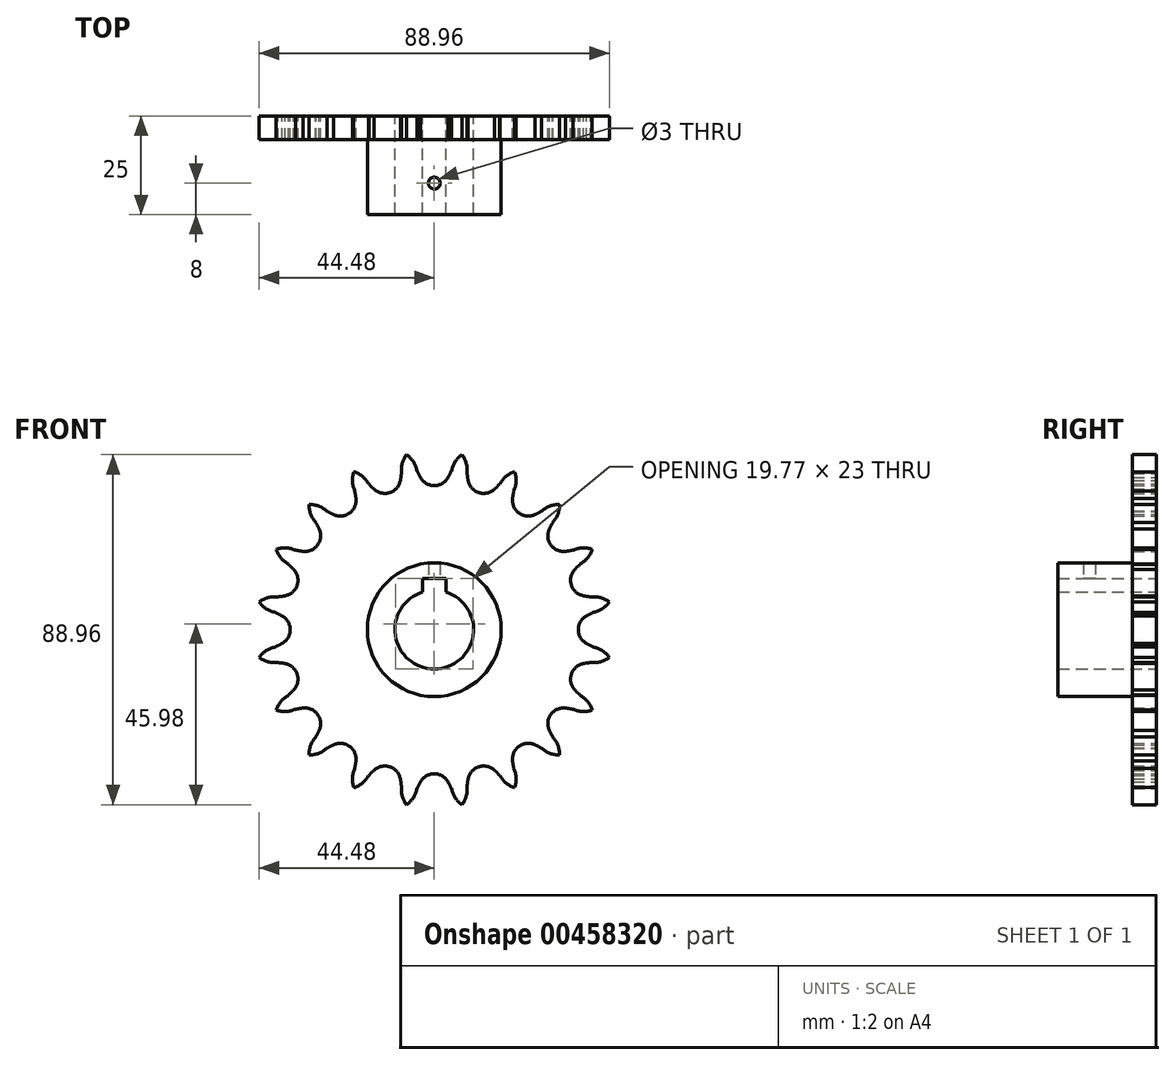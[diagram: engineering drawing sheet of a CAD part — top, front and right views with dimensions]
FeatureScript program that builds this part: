
annotation { "Feature Type Name" : "Feature", "Feature Type Description" : "" }
export const myFeature = defineFeature(function(context is Context, id is Id, definition is map)
    precondition{}
    {
        {
            var Q0;
            Q0=qCreatedBy(makeId("Front.planeOp"),FACE);
            var sketch = newSketch(context, id + "F0", { "sketchPlane" : qUnion([Q0])});
            skCircle(sketch, "E0", {"center": v(0, 0) * mm, "radius": 17 * mm});
            skCircle(sketch, "E1", {"center": v(0, 0) * mm, "radius": 40.6 * mm});
            skLineSegment(sketch, "E2", {"start": v(0, 0) * mm, "end": v(0, 40.6) * mm, "construction": true});
            skArc(sketch, "E3", {"start": v(3.98, 40.4) * mm, "mid": v(3.98, 40.5) * mm, "end": v(3.98, 40.6) * mm});
            skLineSegment(sketch, "E4", {"start": v(0, 40.6) * mm, "end": v(42.62, 40.6) * mm, "construction": true});
            skLineSegment(sketch, "E5", {"start": v(0, 40.6) * mm, "end": v(4.45, 44.07) * mm, "construction": true});
            skArc(sketch, "E6", {"start": v(-4.39, 40.35) * mm, "mid": v(-5.32, 42.68) * mm, "end": v(-7.05, 44.48) * mm});
            skLineSegment(sketch, "E7", {"start": v(4.45, 44.07) * mm, "end": v(-4.39, 40.35) * mm, "construction": true});
            skLineSegment(sketch, "E8", {"start": v(0, 0) * mm, "end": v(-7.48, 47.24) * mm, "construction": true});
            skLineSegment(sketch, "E9", {"start": v(4.45, 44.07) * mm, "end": v(-3.14, 38.14) * mm, "construction": true});
            skArc(sketch, "E10.trimOffspring", {"start": v(3.14, 43.04) * mm, "mid": v(3, 43.22) * mm, "end": v(2.83, 43.39) * mm});
            skArc(sketch, "E11.trimOffspring", {"start": v(-3.98, 40.52) * mm, "mid": v(-3.98, 40.46) * mm, "end": v(-3.98, 40.4) * mm});
            skArc(sketch, "E12.trimOffspring", {"start": v(-3.5, 38.7) * mm, "mid": v(-2.04, 37.17) * mm, "end": v(0, 36.61) * mm});
            skArc(sketch, "E13.trimOffspring", {"start": v(-4.56, 41.04) * mm, "mid": v(-3.96, 39.54) * mm, "end": v(-3.14, 38.14) * mm});
            skArc(sketch, "E14.MirrorCS", {"start": v(3.5, 38.7) * mm, "mid": v(2.04, 37.17) * mm, "end": v(0, 36.61) * mm});
            skArc(sketch, "E15.MirrorCS", {"start": v(4.56, 41.04) * mm, "mid": v(3.96, 39.54) * mm, "end": v(3.14, 38.14) * mm});
            skArc(sketch, "E16.MirrorCS", {"start": v(4.39, 40.35) * mm, "mid": v(5.32, 42.68) * mm, "end": v(7.05, 44.48) * mm});
            skArc(sketch, "E17.1.0", {"start": v(-8.3, 39.73) * mm, "mid": v(-8.13, 42.23) * mm, "end": v(-7.05, 44.48) * mm});
            skArc(sketch, "E17.1.1", {"start": v(-8.35, 40.44) * mm, "mid": v(-8.45, 38.83) * mm, "end": v(-8.8, 37.24) * mm});
            skArc(sketch, "E17.1.2", {"start": v(-8.63, 37.88) * mm, "mid": v(-9.55, 35.98) * mm, "end": v(-11.31, 34.82) * mm});
            skArc(sketch, "E17.1.3", {"start": v(-15.29, 35.72) * mm, "mid": v(-13.42, 34.72) * mm, "end": v(-11.31, 34.82) * mm});
            skArc(sketch, "E17.1.4", {"start": v(-17.02, 37.63) * mm, "mid": v(-15.99, 36.38) * mm, "end": v(-14.77, 35.3) * mm});
            skArc(sketch, "E17.1.5", {"start": v(-16.64, 37.02) * mm, "mid": v(-18.24, 38.94) * mm, "end": v(-20.45, 40.13) * mm});
            skArc(sketch, "E17.2.0", {"start": v(-20.17, 35.23) * mm, "mid": v(-20.78, 37.65) * mm, "end": v(-20.45, 40.13) * mm});
            skArc(sketch, "E17.2.1", {"start": v(-20.44, 35.88) * mm, "mid": v(-20.03, 34.31) * mm, "end": v(-19.88, 32.7) * mm});
            skArc(sketch, "E17.2.2", {"start": v(-19.91, 33.36) * mm, "mid": v(-20.2, 31.27) * mm, "end": v(-21.52, 29.62) * mm});
            skArc(sketch, "E17.2.3", {"start": v(-25.58, 29.25) * mm, "mid": v(-23.5, 28.87) * mm, "end": v(-21.52, 29.62) * mm});
            skArc(sketch, "E17.2.4", {"start": v(-27.81, 30.53) * mm, "mid": v(-26.44, 29.66) * mm, "end": v(-24.96, 29.01) * mm});
            skArc(sketch, "E17.2.5", {"start": v(-27.27, 30.07) * mm, "mid": v(-29.38, 31.4) * mm, "end": v(-31.85, 31.85) * mm});
            skArc(sketch, "E17.3.0", {"start": v(-30.07, 27.27) * mm, "mid": v(-31.4, 29.38) * mm, "end": v(-31.85, 31.85) * mm});
            skArc(sketch, "E17.3.1", {"start": v(-30.53, 27.81) * mm, "mid": v(-29.66, 26.44) * mm, "end": v(-29.01, 24.96) * mm});
            skArc(sketch, "E17.3.2", {"start": v(-29.25, 25.58) * mm, "mid": v(-28.87, 23.5) * mm, "end": v(-29.62, 21.52) * mm});
            skArc(sketch, "E17.3.3", {"start": v(-33.36, 19.91) * mm, "mid": v(-31.27, 20.2) * mm, "end": v(-29.62, 21.52) * mm});
            skArc(sketch, "E17.3.4", {"start": v(-35.88, 20.44) * mm, "mid": v(-34.31, 20.03) * mm, "end": v(-32.7, 19.88) * mm});
            skArc(sketch, "E17.3.5", {"start": v(-35.23, 20.17) * mm, "mid": v(-37.65, 20.78) * mm, "end": v(-40.13, 20.45) * mm});
            skArc(sketch, "E17.4.0", {"start": v(-37.02, 16.64) * mm, "mid": v(-38.94, 18.24) * mm, "end": v(-40.13, 20.45) * mm});
            skArc(sketch, "E17.4.1", {"start": v(-37.63, 17.02) * mm, "mid": v(-36.38, 15.99) * mm, "end": v(-35.3, 14.77) * mm});
            skArc(sketch, "E17.4.2", {"start": v(-35.72, 15.29) * mm, "mid": v(-34.72, 13.42) * mm, "end": v(-34.82, 11.31) * mm});
            skArc(sketch, "E17.4.3", {"start": v(-37.88, 8.63) * mm, "mid": v(-35.98, 9.55) * mm, "end": v(-34.82, 11.31) * mm});
            skArc(sketch, "E17.4.4", {"start": v(-40.44, 8.35) * mm, "mid": v(-38.83, 8.45) * mm, "end": v(-37.24, 8.8) * mm});
            skArc(sketch, "E17.4.5", {"start": v(-39.73, 8.3) * mm, "mid": v(-42.23, 8.13) * mm, "end": v(-44.48, 7.05) * mm});
            skArc(sketch, "E17.5.0", {"start": v(-40.35, 4.39) * mm, "mid": v(-42.68, 5.32) * mm, "end": v(-44.48, 7.05) * mm});
            skArc(sketch, "E17.5.1", {"start": v(-41.04, 4.56) * mm, "mid": v(-39.54, 3.96) * mm, "end": v(-38.14, 3.14) * mm});
            skArc(sketch, "E17.5.2", {"start": v(-38.7, 3.5) * mm, "mid": v(-37.17, 2.04) * mm, "end": v(-36.61, 0) * mm});
            skArc(sketch, "E17.5.3", {"start": v(-38.7, -3.5) * mm, "mid": v(-37.17, -2.04) * mm, "end": v(-36.61, 0) * mm});
            skArc(sketch, "E17.5.4", {"start": v(-41.04, -4.56) * mm, "mid": v(-39.54, -3.96) * mm, "end": v(-38.14, -3.14) * mm});
            skArc(sketch, "E17.5.5", {"start": v(-40.35, -4.39) * mm, "mid": v(-42.68, -5.32) * mm, "end": v(-44.48, -7.05) * mm});
            skArc(sketch, "E17.6.0", {"start": v(-39.73, -8.3) * mm, "mid": v(-42.23, -8.13) * mm, "end": v(-44.48, -7.05) * mm});
            skArc(sketch, "E17.6.1", {"start": v(-40.44, -8.35) * mm, "mid": v(-38.83, -8.45) * mm, "end": v(-37.24, -8.8) * mm});
            skArc(sketch, "E17.6.2", {"start": v(-37.88, -8.63) * mm, "mid": v(-35.98, -9.55) * mm, "end": v(-34.82, -11.31) * mm});
            skArc(sketch, "E17.6.3", {"start": v(-35.72, -15.29) * mm, "mid": v(-34.72, -13.42) * mm, "end": v(-34.82, -11.31) * mm});
            skArc(sketch, "E17.6.4", {"start": v(-37.63, -17.02) * mm, "mid": v(-36.38, -15.99) * mm, "end": v(-35.3, -14.77) * mm});
            skArc(sketch, "E17.6.5", {"start": v(-37.02, -16.64) * mm, "mid": v(-38.94, -18.24) * mm, "end": v(-40.13, -20.45) * mm});
            skArc(sketch, "E17.7.0", {"start": v(-35.23, -20.17) * mm, "mid": v(-37.65, -20.78) * mm, "end": v(-40.13, -20.45) * mm});
            skArc(sketch, "E17.7.1", {"start": v(-35.88, -20.44) * mm, "mid": v(-34.31, -20.03) * mm, "end": v(-32.7, -19.88) * mm});
            skArc(sketch, "E17.7.2", {"start": v(-33.36, -19.91) * mm, "mid": v(-31.27, -20.2) * mm, "end": v(-29.62, -21.52) * mm});
            skArc(sketch, "E17.7.3", {"start": v(-29.25, -25.58) * mm, "mid": v(-28.87, -23.5) * mm, "end": v(-29.62, -21.52) * mm});
            skArc(sketch, "E17.7.4", {"start": v(-30.53, -27.81) * mm, "mid": v(-29.66, -26.44) * mm, "end": v(-29.01, -24.96) * mm});
            skArc(sketch, "E17.7.5", {"start": v(-30.07, -27.27) * mm, "mid": v(-31.4, -29.38) * mm, "end": v(-31.85, -31.85) * mm});
            skArc(sketch, "E17.8.0", {"start": v(-27.27, -30.07) * mm, "mid": v(-29.38, -31.4) * mm, "end": v(-31.85, -31.85) * mm});
            skArc(sketch, "E17.8.1", {"start": v(-27.81, -30.53) * mm, "mid": v(-26.44, -29.66) * mm, "end": v(-24.96, -29.01) * mm});
            skArc(sketch, "E17.8.2", {"start": v(-25.58, -29.25) * mm, "mid": v(-23.5, -28.87) * mm, "end": v(-21.52, -29.62) * mm});
            skArc(sketch, "E17.8.3", {"start": v(-19.91, -33.36) * mm, "mid": v(-20.2, -31.27) * mm, "end": v(-21.52, -29.62) * mm});
            skArc(sketch, "E17.8.4", {"start": v(-20.44, -35.88) * mm, "mid": v(-20.03, -34.31) * mm, "end": v(-19.88, -32.7) * mm});
            skArc(sketch, "E17.8.5", {"start": v(-20.17, -35.23) * mm, "mid": v(-20.78, -37.65) * mm, "end": v(-20.45, -40.13) * mm});
            skArc(sketch, "E17.9.0", {"start": v(-16.64, -37.02) * mm, "mid": v(-18.24, -38.94) * mm, "end": v(-20.45, -40.13) * mm});
            skArc(sketch, "E17.9.1", {"start": v(-17.02, -37.63) * mm, "mid": v(-15.99, -36.38) * mm, "end": v(-14.77, -35.3) * mm});
            skArc(sketch, "E17.9.2", {"start": v(-15.29, -35.72) * mm, "mid": v(-13.42, -34.72) * mm, "end": v(-11.31, -34.82) * mm});
            skArc(sketch, "E17.9.3", {"start": v(-8.63, -37.88) * mm, "mid": v(-9.55, -35.98) * mm, "end": v(-11.31, -34.82) * mm});
            skArc(sketch, "E17.9.4", {"start": v(-8.35, -40.44) * mm, "mid": v(-8.45, -38.83) * mm, "end": v(-8.8, -37.24) * mm});
            skArc(sketch, "E17.9.5", {"start": v(-8.3, -39.73) * mm, "mid": v(-8.13, -42.23) * mm, "end": v(-7.05, -44.48) * mm});
            skArc(sketch, "E17.10.0", {"start": v(-4.39, -40.35) * mm, "mid": v(-5.32, -42.68) * mm, "end": v(-7.05, -44.48) * mm});
            skArc(sketch, "E17.10.1", {"start": v(-4.56, -41.04) * mm, "mid": v(-3.96, -39.54) * mm, "end": v(-3.14, -38.14) * mm});
            skArc(sketch, "E17.10.2", {"start": v(-3.5, -38.7) * mm, "mid": v(-2.04, -37.17) * mm, "end": v(0, -36.61) * mm});
            skArc(sketch, "E17.10.3", {"start": v(3.5, -38.7) * mm, "mid": v(2.04, -37.17) * mm, "end": v(0, -36.61) * mm});
            skArc(sketch, "E17.10.4", {"start": v(4.56, -41.04) * mm, "mid": v(3.96, -39.54) * mm, "end": v(3.14, -38.14) * mm});
            skArc(sketch, "E17.10.5", {"start": v(4.39, -40.35) * mm, "mid": v(5.32, -42.68) * mm, "end": v(7.05, -44.48) * mm});
            skArc(sketch, "E17.11.0", {"start": v(8.3, -39.73) * mm, "mid": v(8.13, -42.23) * mm, "end": v(7.05, -44.48) * mm});
            skArc(sketch, "E17.11.1", {"start": v(8.35, -40.44) * mm, "mid": v(8.45, -38.83) * mm, "end": v(8.8, -37.24) * mm});
            skArc(sketch, "E17.11.2", {"start": v(8.63, -37.88) * mm, "mid": v(9.55, -35.98) * mm, "end": v(11.31, -34.82) * mm});
            skArc(sketch, "E17.11.3", {"start": v(15.29, -35.72) * mm, "mid": v(13.42, -34.72) * mm, "end": v(11.31, -34.82) * mm});
            skArc(sketch, "E17.11.4", {"start": v(17.02, -37.63) * mm, "mid": v(15.99, -36.38) * mm, "end": v(14.77, -35.3) * mm});
            skArc(sketch, "E17.11.5", {"start": v(16.64, -37.02) * mm, "mid": v(18.24, -38.94) * mm, "end": v(20.45, -40.13) * mm});
            skArc(sketch, "E17.12.0", {"start": v(20.17, -35.23) * mm, "mid": v(20.78, -37.65) * mm, "end": v(20.45, -40.13) * mm});
            skArc(sketch, "E17.12.1", {"start": v(20.44, -35.88) * mm, "mid": v(20.03, -34.31) * mm, "end": v(19.88, -32.7) * mm});
            skArc(sketch, "E17.12.2", {"start": v(19.91, -33.36) * mm, "mid": v(20.2, -31.27) * mm, "end": v(21.52, -29.62) * mm});
            skArc(sketch, "E17.12.3", {"start": v(25.58, -29.25) * mm, "mid": v(23.5, -28.87) * mm, "end": v(21.52, -29.62) * mm});
            skArc(sketch, "E17.12.4", {"start": v(27.81, -30.53) * mm, "mid": v(26.44, -29.66) * mm, "end": v(24.96, -29.01) * mm});
            skArc(sketch, "E17.12.5", {"start": v(27.27, -30.07) * mm, "mid": v(29.38, -31.4) * mm, "end": v(31.85, -31.85) * mm});
            skArc(sketch, "E17.13.0", {"start": v(30.07, -27.27) * mm, "mid": v(31.4, -29.38) * mm, "end": v(31.85, -31.85) * mm});
            skArc(sketch, "E17.13.1", {"start": v(30.53, -27.81) * mm, "mid": v(29.66, -26.44) * mm, "end": v(29.01, -24.96) * mm});
            skArc(sketch, "E17.13.2", {"start": v(29.25, -25.58) * mm, "mid": v(28.87, -23.5) * mm, "end": v(29.62, -21.52) * mm});
            skArc(sketch, "E17.13.3", {"start": v(33.36, -19.91) * mm, "mid": v(31.27, -20.2) * mm, "end": v(29.62, -21.52) * mm});
            skArc(sketch, "E17.13.4", {"start": v(35.88, -20.44) * mm, "mid": v(34.31, -20.03) * mm, "end": v(32.7, -19.88) * mm});
            skArc(sketch, "E17.13.5", {"start": v(35.23, -20.17) * mm, "mid": v(37.65, -20.78) * mm, "end": v(40.13, -20.45) * mm});
            skArc(sketch, "E17.14.0", {"start": v(37.02, -16.64) * mm, "mid": v(38.94, -18.24) * mm, "end": v(40.13, -20.45) * mm});
            skArc(sketch, "E17.14.1", {"start": v(37.63, -17.02) * mm, "mid": v(36.38, -15.99) * mm, "end": v(35.3, -14.77) * mm});
            skArc(sketch, "E17.14.2", {"start": v(35.72, -15.29) * mm, "mid": v(34.72, -13.42) * mm, "end": v(34.82, -11.31) * mm});
            skArc(sketch, "E17.14.3", {"start": v(37.88, -8.63) * mm, "mid": v(35.98, -9.55) * mm, "end": v(34.82, -11.31) * mm});
            skArc(sketch, "E17.14.4", {"start": v(40.44, -8.35) * mm, "mid": v(38.83, -8.45) * mm, "end": v(37.24, -8.8) * mm});
            skArc(sketch, "E17.14.5", {"start": v(39.73, -8.3) * mm, "mid": v(42.23, -8.13) * mm, "end": v(44.48, -7.05) * mm});
            skArc(sketch, "E17.15.0", {"start": v(40.35, -4.39) * mm, "mid": v(42.68, -5.32) * mm, "end": v(44.48, -7.05) * mm});
            skArc(sketch, "E17.15.1", {"start": v(41.04, -4.56) * mm, "mid": v(39.54, -3.96) * mm, "end": v(38.14, -3.14) * mm});
            skArc(sketch, "E17.15.2", {"start": v(38.7, -3.5) * mm, "mid": v(37.17, -2.04) * mm, "end": v(36.61, 0) * mm});
            skArc(sketch, "E17.15.3", {"start": v(38.7, 3.5) * mm, "mid": v(37.17, 2.04) * mm, "end": v(36.61, 0) * mm});
            skArc(sketch, "E17.15.4", {"start": v(41.04, 4.56) * mm, "mid": v(39.54, 3.96) * mm, "end": v(38.14, 3.14) * mm});
            skArc(sketch, "E17.15.5", {"start": v(40.35, 4.39) * mm, "mid": v(42.68, 5.32) * mm, "end": v(44.48, 7.05) * mm});
            skArc(sketch, "E17.16.0", {"start": v(39.73, 8.3) * mm, "mid": v(42.23, 8.13) * mm, "end": v(44.48, 7.05) * mm});
            skArc(sketch, "E17.16.1", {"start": v(40.44, 8.35) * mm, "mid": v(38.83, 8.45) * mm, "end": v(37.24, 8.8) * mm});
            skArc(sketch, "E17.16.2", {"start": v(37.88, 8.63) * mm, "mid": v(35.98, 9.55) * mm, "end": v(34.82, 11.31) * mm});
            skArc(sketch, "E17.16.3", {"start": v(35.72, 15.29) * mm, "mid": v(34.72, 13.42) * mm, "end": v(34.82, 11.31) * mm});
            skArc(sketch, "E17.16.4", {"start": v(37.63, 17.02) * mm, "mid": v(36.38, 15.99) * mm, "end": v(35.3, 14.77) * mm});
            skArc(sketch, "E17.16.5", {"start": v(37.02, 16.64) * mm, "mid": v(38.94, 18.24) * mm, "end": v(40.13, 20.45) * mm});
            skArc(sketch, "E17.17.0", {"start": v(35.23, 20.17) * mm, "mid": v(37.65, 20.78) * mm, "end": v(40.13, 20.45) * mm});
            skArc(sketch, "E17.17.1", {"start": v(35.88, 20.44) * mm, "mid": v(34.31, 20.03) * mm, "end": v(32.7, 19.88) * mm});
            skArc(sketch, "E17.17.2", {"start": v(33.36, 19.91) * mm, "mid": v(31.27, 20.2) * mm, "end": v(29.62, 21.52) * mm});
            skArc(sketch, "E17.17.3", {"start": v(29.25, 25.58) * mm, "mid": v(28.87, 23.5) * mm, "end": v(29.62, 21.52) * mm});
            skArc(sketch, "E17.17.4", {"start": v(30.53, 27.81) * mm, "mid": v(29.66, 26.44) * mm, "end": v(29.01, 24.96) * mm});
            skArc(sketch, "E17.17.5", {"start": v(30.07, 27.27) * mm, "mid": v(31.4, 29.38) * mm, "end": v(31.85, 31.85) * mm});
            skArc(sketch, "E17.18.0", {"start": v(27.27, 30.07) * mm, "mid": v(29.38, 31.4) * mm, "end": v(31.85, 31.85) * mm});
            skArc(sketch, "E17.18.1", {"start": v(27.81, 30.53) * mm, "mid": v(26.44, 29.66) * mm, "end": v(24.96, 29.01) * mm});
            skArc(sketch, "E17.18.2", {"start": v(25.58, 29.25) * mm, "mid": v(23.5, 28.87) * mm, "end": v(21.52, 29.62) * mm});
            skArc(sketch, "E17.18.3", {"start": v(19.91, 33.36) * mm, "mid": v(20.2, 31.27) * mm, "end": v(21.52, 29.62) * mm});
            skArc(sketch, "E17.18.4", {"start": v(20.44, 35.88) * mm, "mid": v(20.03, 34.31) * mm, "end": v(19.88, 32.7) * mm});
            skArc(sketch, "E17.18.5", {"start": v(20.17, 35.23) * mm, "mid": v(20.78, 37.65) * mm, "end": v(20.45, 40.13) * mm});
            skArc(sketch, "E17.19.0", {"start": v(16.64, 37.02) * mm, "mid": v(18.24, 38.94) * mm, "end": v(20.45, 40.13) * mm});
            skArc(sketch, "E17.19.1", {"start": v(17.02, 37.63) * mm, "mid": v(15.99, 36.38) * mm, "end": v(14.77, 35.3) * mm});
            skArc(sketch, "E17.19.2", {"start": v(15.29, 35.72) * mm, "mid": v(13.42, 34.72) * mm, "end": v(11.31, 34.82) * mm});
            skArc(sketch, "E17.19.3", {"start": v(8.63, 37.88) * mm, "mid": v(9.55, 35.98) * mm, "end": v(11.31, 34.82) * mm});
            skArc(sketch, "E17.19.4", {"start": v(8.35, 40.44) * mm, "mid": v(8.45, 38.83) * mm, "end": v(8.8, 37.24) * mm});
            skArc(sketch, "E17.19.5", {"start": v(8.3, 39.73) * mm, "mid": v(8.13, 42.23) * mm, "end": v(7.05, 44.48) * mm});
            skCircle(sketch, "E18", {"center": v(0, 0) * mm, "radius": 10 * mm});
            skLineSegment(sketch, "E19.bottom", {"start": v(-3, 13) * mm, "end": v(3, 13) * mm});
            skLineSegment(sketch, "E19.top", {"start": v(-3, 9) * mm, "end": v(3, 9) * mm});
            skLineSegment(sketch, "E19.left", {"start": v(-3, 13) * mm, "end": v(-3, 9) * mm});
            skLineSegment(sketch, "E19.right", {"start": v(3, 13) * mm, "end": v(3, 9) * mm});
            skSolve(sketch);
        }
        {
            var Q0;
            Q0=makeQuery(id+"F0.imprint","IMPRINT",FACE,{"disambiguationData":[TD([[makeQuery(id+"F0.imprint","IMPRINT",EDGE,{"derivedFrom":sQuery(id+"F0.wireOp",EDGE,"E0")}),1.0]])]});
            extrude(context, id + "F1", {"entities" : qUnion([Q0]), "depth" : 25 * mm, "offsetDistance" : 25 * mm});
        }
        {
            var Q0;
            Q0=makeQuery(id+"F0.imprint","IMPRINT",FACE,{"disambiguationData":[TD([[makeQuery(id+"F0.imprint","IMPRINT",EDGE,{"derivedFrom":sQuery(id+"F0.wireOp",EDGE,"E0")}),-1.0]])]});
            var Q1;
            {var subQ1=sQuery(id+"F0.wireOp",EDGE,"E1");var subQ4=sQuery(id+"F0.wireOp",EDGE,"E17.6.5");var subQ7=makeQuery(id+"F0.imprint","INTERSECT",VERTEX,{"derivedFrom":[subQ1,subQ4]});Q1=makeQuery(id+"F0.imprint","IMPRINT",FACE,{"disambiguationData":[TD([[makeQuery(id+"F0.imprint","IMPRINT",EDGE,{"disambiguationData":[TD([[subQ7,-1.0]])],"derivedFrom":subQ1}),-1.0]])]});}
            var Q2;
            {var subQ1=sQuery(id+"F0.wireOp",EDGE,"E1");var subQ4=sQuery(id+"F0.wireOp",EDGE,"E17.7.5");var subQ5=makeQuery(id+"F0.imprint","INTERSECT",VERTEX,{"derivedFrom":[subQ1,subQ4]});Q2=makeQuery(id+"F0.imprint","IMPRINT",FACE,{"disambiguationData":[TD([[makeQuery(id+"F0.imprint","IMPRINT",EDGE,{"disambiguationData":[TD([[subQ5,-1.0]])],"derivedFrom":subQ1}),-1.0]])]});}
            var Q3;
            {var subQ1=sQuery(id+"F0.wireOp",EDGE,"E1");var subQ4=sQuery(id+"F0.wireOp",EDGE,"E17.8.5");var subQ7=makeQuery(id+"F0.imprint","INTERSECT",VERTEX,{"derivedFrom":[subQ1,subQ4]});Q3=makeQuery(id+"F0.imprint","IMPRINT",FACE,{"disambiguationData":[TD([[makeQuery(id+"F0.imprint","IMPRINT",EDGE,{"disambiguationData":[TD([[subQ7,-1.0]])],"derivedFrom":subQ1}),-1.0]])]});}
            var Q4;
            {var subQ1=sQuery(id+"F0.wireOp",EDGE,"E1");var subQ4=sQuery(id+"F0.wireOp",EDGE,"E17.10.5");var subQ7=makeQuery(id+"F0.imprint","INTERSECT",VERTEX,{"derivedFrom":[subQ1,subQ4]});Q4=makeQuery(id+"F0.imprint","IMPRINT",FACE,{"disambiguationData":[TD([[makeQuery(id+"F0.imprint","IMPRINT",EDGE,{"disambiguationData":[TD([[subQ7,-1.0]])],"derivedFrom":subQ1}),-1.0]])]});}
            var Q5;
            {var subQ1=sQuery(id+"F0.wireOp",EDGE,"E1");var subQ4=sQuery(id+"F0.wireOp",EDGE,"E17.11.5");var subQ7=makeQuery(id+"F0.imprint","INTERSECT",VERTEX,{"derivedFrom":[subQ1,subQ4]});Q5=makeQuery(id+"F0.imprint","IMPRINT",FACE,{"disambiguationData":[TD([[makeQuery(id+"F0.imprint","IMPRINT",EDGE,{"disambiguationData":[TD([[subQ7,-1.0]])],"derivedFrom":subQ1}),-1.0]])]});}
            var Q6;
            {var subQ1=sQuery(id+"F0.wireOp",EDGE,"E1");var subQ4=sQuery(id+"F0.wireOp",EDGE,"E17.12.5");var subQ7=makeQuery(id+"F0.imprint","INTERSECT",VERTEX,{"derivedFrom":[subQ1,subQ4]});Q6=makeQuery(id+"F0.imprint","IMPRINT",FACE,{"disambiguationData":[TD([[makeQuery(id+"F0.imprint","IMPRINT",EDGE,{"disambiguationData":[TD([[subQ7,-1.0]])],"derivedFrom":subQ1}),-1.0]])]});}
            var Q7;
            {var subQ1=sQuery(id+"F0.wireOp",EDGE,"E1");var subQ4=sQuery(id+"F0.wireOp",EDGE,"E17.13.5");var subQ7=makeQuery(id+"F0.imprint","INTERSECT",VERTEX,{"derivedFrom":[subQ1,subQ4]});Q7=makeQuery(id+"F0.imprint","IMPRINT",FACE,{"disambiguationData":[TD([[makeQuery(id+"F0.imprint","IMPRINT",EDGE,{"disambiguationData":[TD([[subQ7,-1.0]])],"derivedFrom":subQ1}),-1.0]])]});}
            var Q8;
            {var subQ1=sQuery(id+"F0.wireOp",EDGE,"E1");var subQ4=sQuery(id+"F0.wireOp",EDGE,"E17.9.5");var subQ7=makeQuery(id+"F0.imprint","INTERSECT",VERTEX,{"derivedFrom":[subQ1,subQ4]});Q8=makeQuery(id+"F0.imprint","IMPRINT",FACE,{"disambiguationData":[TD([[makeQuery(id+"F0.imprint","IMPRINT",EDGE,{"disambiguationData":[TD([[subQ7,-1.0]])],"derivedFrom":subQ1}),-1.0]])]});}
            var Q9;
            {var subQ1=sQuery(id+"F0.wireOp",EDGE,"E1");var subQ4=sQuery(id+"F0.wireOp",EDGE,"E17.14.5");var subQ7=makeQuery(id+"F0.imprint","INTERSECT",VERTEX,{"derivedFrom":[subQ1,subQ4]});Q9=makeQuery(id+"F0.imprint","IMPRINT",FACE,{"disambiguationData":[TD([[makeQuery(id+"F0.imprint","IMPRINT",EDGE,{"disambiguationData":[TD([[subQ7,-1.0]])],"derivedFrom":subQ1}),-1.0]])]});}
            var Q10;
            {var subQ0=sQuery(id+"F0.wireOp",EDGE,"E17.15.5");var subQ4=sQuery(id+"F0.wireOp",EDGE,"E1");var subQ5=makeQuery(id+"F0.imprint","INTERSECT",VERTEX,{"derivedFrom":[subQ4,subQ0]});Q10=makeQuery(id+"F0.imprint","IMPRINT",FACE,{"disambiguationData":[TD([[makeQuery(id+"F0.imprint","IMPRINT",EDGE,{"disambiguationData":[TD([[subQ5,-1.0]])],"derivedFrom":subQ4}),-1.0]])]});}
            var Q11;
            {var subQ0=sQuery(id+"F0.wireOp",EDGE,"E17.16.5");var subQ4=sQuery(id+"F0.wireOp",EDGE,"E1");var subQ5=makeQuery(id+"F0.imprint","INTERSECT",VERTEX,{"derivedFrom":[subQ4,subQ0]});Q11=makeQuery(id+"F0.imprint","IMPRINT",FACE,{"disambiguationData":[TD([[makeQuery(id+"F0.imprint","IMPRINT",EDGE,{"disambiguationData":[TD([[subQ5,-1.0]])],"derivedFrom":subQ4}),-1.0]])]});}
            var Q12;
            {var subQ0=sQuery(id+"F0.wireOp",EDGE,"E17.17.5");var subQ4=sQuery(id+"F0.wireOp",EDGE,"E1");var subQ5=makeQuery(id+"F0.imprint","INTERSECT",VERTEX,{"derivedFrom":[subQ4,subQ0]});Q12=makeQuery(id+"F0.imprint","IMPRINT",FACE,{"disambiguationData":[TD([[makeQuery(id+"F0.imprint","IMPRINT",EDGE,{"disambiguationData":[TD([[subQ5,-1.0]])],"derivedFrom":subQ4}),-1.0]])]});}
            var Q13;
            {var subQ0=sQuery(id+"F0.wireOp",EDGE,"E17.18.5");var subQ4=sQuery(id+"F0.wireOp",EDGE,"E1");var subQ5=makeQuery(id+"F0.imprint","INTERSECT",VERTEX,{"derivedFrom":[subQ4,subQ0]});Q13=makeQuery(id+"F0.imprint","IMPRINT",FACE,{"disambiguationData":[TD([[makeQuery(id+"F0.imprint","IMPRINT",EDGE,{"disambiguationData":[TD([[subQ5,-1.0]])],"derivedFrom":subQ4}),-1.0]])]});}
            var Q14;
            {var subQ2=sQuery(id+"F0.wireOp",EDGE,"E1");var subQ4=sQuery(id+"F0.wireOp",EDGE,"E16.MirrorCS");var subQ7=makeQuery(id+"F0.imprint","INTERSECT",VERTEX,{"derivedFrom":[subQ2,subQ4]});Q14=makeQuery(id+"F0.imprint","IMPRINT",FACE,{"disambiguationData":[TD([[makeQuery(id+"F0.imprint","IMPRINT",EDGE,{"disambiguationData":[TD([[subQ7,1.0]])],"derivedFrom":subQ2}),-1.0]])]});}
            var Q15;
            {var subQ1=sQuery(id+"F0.wireOp",EDGE,"E1");var subQ4=sQuery(id+"F0.wireOp",EDGE,"E17.1.5");var subQ7=makeQuery(id+"F0.imprint","INTERSECT",VERTEX,{"derivedFrom":[subQ1,subQ4]});Q15=makeQuery(id+"F0.imprint","IMPRINT",FACE,{"disambiguationData":[TD([[makeQuery(id+"F0.imprint","IMPRINT",EDGE,{"disambiguationData":[TD([[subQ7,-1.0]])],"derivedFrom":subQ1}),-1.0]])]});}
            var Q16;
            {var subQ1=sQuery(id+"F0.wireOp",EDGE,"E1");var subQ4=sQuery(id+"F0.wireOp",EDGE,"E17.2.5");var subQ7=makeQuery(id+"F0.imprint","INTERSECT",VERTEX,{"derivedFrom":[subQ1,subQ4]});Q16=makeQuery(id+"F0.imprint","IMPRINT",FACE,{"disambiguationData":[TD([[makeQuery(id+"F0.imprint","IMPRINT",EDGE,{"disambiguationData":[TD([[subQ7,-1.0]])],"derivedFrom":subQ1}),-1.0]])]});}
            var Q17;
            {var subQ1=sQuery(id+"F0.wireOp",EDGE,"E1");var subQ4=sQuery(id+"F0.wireOp",EDGE,"E17.3.5");var subQ7=makeQuery(id+"F0.imprint","INTERSECT",VERTEX,{"derivedFrom":[subQ1,subQ4]});Q17=makeQuery(id+"F0.imprint","IMPRINT",FACE,{"disambiguationData":[TD([[makeQuery(id+"F0.imprint","IMPRINT",EDGE,{"disambiguationData":[TD([[subQ7,-1.0]])],"derivedFrom":subQ1}),-1.0]])]});}
            var Q18;
            {var subQ1=sQuery(id+"F0.wireOp",EDGE,"E1");var subQ4=sQuery(id+"F0.wireOp",EDGE,"E17.4.5");var subQ7=makeQuery(id+"F0.imprint","INTERSECT",VERTEX,{"derivedFrom":[subQ1,subQ4]});Q18=makeQuery(id+"F0.imprint","IMPRINT",FACE,{"disambiguationData":[TD([[makeQuery(id+"F0.imprint","IMPRINT",EDGE,{"disambiguationData":[TD([[subQ7,-1.0]])],"derivedFrom":subQ1}),-1.0]])]});}
            var Q19;
            {var subQ1=sQuery(id+"F0.wireOp",EDGE,"E1");var subQ4=sQuery(id+"F0.wireOp",EDGE,"E17.5.5");var subQ7=makeQuery(id+"F0.imprint","INTERSECT",VERTEX,{"derivedFrom":[subQ1,subQ4]});Q19=makeQuery(id+"F0.imprint","IMPRINT",FACE,{"disambiguationData":[TD([[makeQuery(id+"F0.imprint","IMPRINT",EDGE,{"disambiguationData":[TD([[subQ7,-1.0]])],"derivedFrom":subQ1}),-1.0]])]});}
            var Q20;
            {var subQ1=sQuery(id+"F0.wireOp",EDGE,"E1");var subQ4=sQuery(id+"F0.wireOp",EDGE,"E6");var subQ5=makeQuery(id+"F0.imprint","INTERSECT",VERTEX,{"derivedFrom":[subQ1,subQ4]});Q20=makeQuery(id+"F0.imprint","IMPRINT",FACE,{"disambiguationData":[TD([[makeQuery(id+"F0.imprint","IMPRINT",EDGE,{"disambiguationData":[TD([[subQ5,-1.0]])],"derivedFrom":subQ1}),-1.0]])]});}
            extrude(context, id + "F2", {"entities" : qUnion([Q0, Q1, Q2, Q3, Q4, Q5, Q6, Q7, Q8, Q9, Q10, Q11, Q12, Q13, Q14, Q15, Q16, Q17, Q18, Q19, Q20]), "operationType" : NewBodyOperationType.ADD, "depth" : 6 * mm, "offsetDistance" : 25 * mm});
        }
        {
            var Q0;
            Q0=makeQuery(id+"F1.opExtrude","SWEPT_FACE",FACE,{"disambiguationData":[OSD([sQuery(id+"F0.wireOp",EDGE,"E19.bottom")])]});
            var sketch = newSketch(context, id + "F3", { "sketchPlane" : qUnion([Q0])});
            skCircle(sketch, "E20", {"center": v(-1.54, -39.53) * mm, "radius": 2.25 * mm});
            skCircle(sketch, "E21", {"center": v(0, 17) * mm, "radius": 1.5 * mm});
            skSolve(sketch);
        }
        {
            var Q0;
            Q0=makeQuery(id+"F3.imprint","IMPRINT",FACE,{"disambiguationData":[TD([[makeQuery(id+"F3.imprint","IMPRINT",EDGE,{"derivedFrom":sQuery(id+"F3.wireOp",EDGE,"E21")}),1.0]])]});
            extrude(context, id + "F4", {"entities" : qUnion([Q0]), "operationType" : NewBodyOperationType.REMOVE, "oppositeDirection" : true, "depth" : 5 * mm, "offsetDistance" : 25 * mm});
        }
    });
